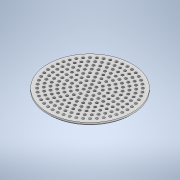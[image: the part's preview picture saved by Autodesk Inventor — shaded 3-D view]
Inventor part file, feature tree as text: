
AUTODESK INVENTOR PART (.ipt)
format: ipt  version: 2022 (Build 260153000, 153)  size: 551,936 bytes
history: native  units: mm
features: extrude x1, chamfer x1, sketch x1
ambient origin geometry x8: Origin, YZ Plane, XZ Plane, XY Plane, X Axis, Y Axis, Z Axis, Center Point
bodies: Solid1 (feature_tree)
feature tree (3):
  extrude  "Extrusion1"  Depth=1.0mm
  chamfer  "Chamfer1"  Distance=1.5mm
  sketch  "Sketch1"  dims[d0=27.0mm d1=0.8mm d2=90.0mm d4=1.5mm d5=10.0mm d7=10.0mm d9=60.0mm d11=360.0deg d13=120.0mm d15=360.0deg d17=180.0mm d19=360.0deg d21=240.0mm d23=360.0deg d25=300.0mm d27=360.0deg d29=360.0mm d31=360.0deg d33=420.0mm d35=360.0deg d37=480.0mm d39=360.0deg d57=1.0mm d58=0.0mm d59=0.5mm d60=2.0mm d61=45.0deg]
